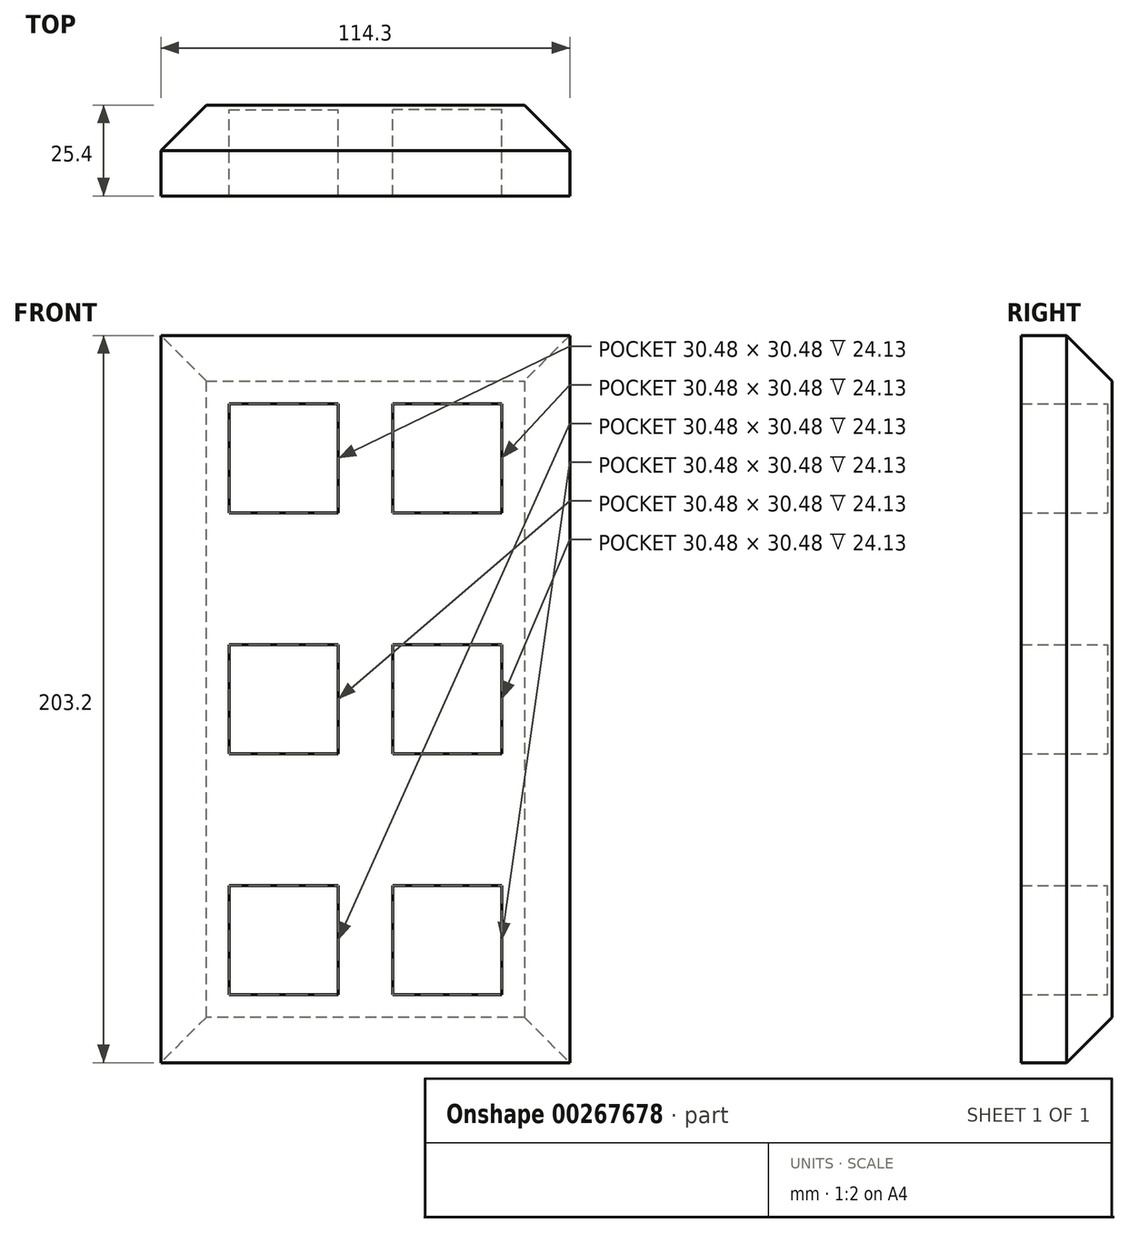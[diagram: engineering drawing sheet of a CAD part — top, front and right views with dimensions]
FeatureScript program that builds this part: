
annotation { "Feature Type Name" : "Feature", "Feature Type Description" : "" }
export const myFeature = defineFeature(function(context is Context, id is Id, definition is map)
    precondition{}
    {
        {
            var Q0;
            Q0=qCreatedBy(makeId("Front.planeOp"),FACE);
            var sketch = newSketch(context, id + "F0", { "sketchPlane" : qUnion([Q0])});
            skLineSegment(sketch, "E0.bottom", {"start": v(57.15, 101.6) * mm, "end": v(-57.15, 101.6) * mm});
            skLineSegment(sketch, "E0.top", {"start": v(57.15, -101.6) * mm, "end": v(-57.15, -101.6) * mm});
            skLineSegment(sketch, "E0.left", {"start": v(57.15, 101.6) * mm, "end": v(57.15, -101.6) * mm});
            skLineSegment(sketch, "E0.right", {"start": v(-57.15, 101.6) * mm, "end": v(-57.15, -101.6) * mm});
            skPoint(sketch, "E0.middle", {"position": v(0, 0) * mm});
            skLineSegment(sketch, "E1", {"start": v(-57.15, 101.6) * mm, "end": v(-38.1, 101.6) * mm});
            skLineSegment(sketch, "E2", {"start": v(-57.15, 101.6) * mm, "end": v(-57.15, 82.55) * mm});
            skLineSegment(sketch, "E3", {"start": v(57.15, 101.6) * mm, "end": v(38.1, 101.6) * mm});
            skLineSegment(sketch, "E4", {"start": v(57.15, 101.6) * mm, "end": v(57.15, 82.55) * mm});
            skLineSegment(sketch, "E5", {"start": v(-57.15, -101.6) * mm, "end": v(-57.15, -82.55) * mm});
            skLineSegment(sketch, "E6", {"start": v(-57.15, -101.6) * mm, "end": v(-38.1, -101.6) * mm});
            skLineSegment(sketch, "E7", {"start": v(57.15, -101.6) * mm, "end": v(57.15, -82.55) * mm});
            skLineSegment(sketch, "E8", {"start": v(57.15, -101.6) * mm, "end": v(38.1, -101.6) * mm});
            skLineSegment(sketch, "E9.bottom", {"start": v(-38.1, 82.55) * mm, "end": v(-7.62, 82.55) * mm});
            skLineSegment(sketch, "E9.top", {"start": v(-38.1, 52.07) * mm, "end": v(-7.62, 52.07) * mm});
            skLineSegment(sketch, "E9.left", {"start": v(-38.1, 82.55) * mm, "end": v(-38.1, 52.07) * mm});
            skLineSegment(sketch, "E9.right", {"start": v(-7.62, 82.55) * mm, "end": v(-7.62, 52.07) * mm});
            skLineSegment(sketch, "E10.bottom", {"start": v(38.1, 82.55) * mm, "end": v(7.62, 82.55) * mm});
            skLineSegment(sketch, "E10.top", {"start": v(38.1, 52.07) * mm, "end": v(7.62, 52.07) * mm});
            skLineSegment(sketch, "E10.left", {"start": v(38.1, 82.55) * mm, "end": v(38.1, 52.07) * mm});
            skLineSegment(sketch, "E10.right", {"start": v(7.62, 82.55) * mm, "end": v(7.62, 52.07) * mm});
            skLineSegment(sketch, "E11.bottom", {"start": v(-38.1, -82.55) * mm, "end": v(-7.62, -82.55) * mm});
            skLineSegment(sketch, "E11.top", {"start": v(-38.1, -52.07) * mm, "end": v(-7.62, -52.07) * mm});
            skLineSegment(sketch, "E11.left", {"start": v(-38.1, -82.55) * mm, "end": v(-38.1, -52.07) * mm});
            skLineSegment(sketch, "E11.right", {"start": v(-7.62, -82.55) * mm, "end": v(-7.62, -52.07) * mm});
            skLineSegment(sketch, "E12.bottom", {"start": v(38.1, -82.55) * mm, "end": v(7.62, -82.55) * mm});
            skLineSegment(sketch, "E12.top", {"start": v(38.1, -52.07) * mm, "end": v(7.62, -52.07) * mm});
            skLineSegment(sketch, "E12.left", {"start": v(38.1, -82.55) * mm, "end": v(38.1, -52.07) * mm});
            skLineSegment(sketch, "E12.right", {"start": v(7.62, -82.55) * mm, "end": v(7.62, -52.07) * mm});
            skLineSegment(sketch, "E13", {"start": v(-57.15, 0) * mm, "end": v(-38.1, 0) * mm});
            skLineSegment(sketch, "E14", {"start": v(57.15, 0) * mm, "end": v(38.1, 0) * mm});
            skLineSegment(sketch, "E15.bottom", {"start": v(-7.62, 15.24) * mm, "end": v(-38.1, 15.24) * mm});
            skLineSegment(sketch, "E15.top", {"start": v(-7.62, -15.24) * mm, "end": v(-38.1, -15.24) * mm});
            skLineSegment(sketch, "E15.left", {"start": v(-7.62, 15.24) * mm, "end": v(-7.62, -15.24) * mm});
            skLineSegment(sketch, "E15.right", {"start": v(-38.1, 15.24) * mm, "end": v(-38.1, -15.24) * mm});
            skPoint(sketch, "E15.middle", {"position": v(-22.86, 0) * mm});
            skPoint(sketch, "E15.middle.positionSnap0", {"position": v(-22.86, 52.07) * mm});
            skPoint(sketch, "E15.centerSnap0", {"position": v(-22.86, 52.07) * mm});
            skLineSegment(sketch, "E16.bottom", {"start": v(7.62, 15.24) * mm, "end": v(38.1, 15.24) * mm});
            skLineSegment(sketch, "E16.top", {"start": v(7.62, -15.24) * mm, "end": v(38.1, -15.24) * mm});
            skLineSegment(sketch, "E16.left", {"start": v(7.62, 15.24) * mm, "end": v(7.62, -15.24) * mm});
            skLineSegment(sketch, "E16.right", {"start": v(38.1, 15.24) * mm, "end": v(38.1, -15.24) * mm});
            skPoint(sketch, "E16.middle", {"position": v(22.86, 0) * mm});
            skPoint(sketch, "E16.middle.positionSnap0", {"position": v(22.86, 52.07) * mm});
            skPoint(sketch, "E16.centerSnap0", {"position": v(22.86, 52.07) * mm});
            skSolve(sketch);
        }
        {
            var Q0;
            Q0=makeQuery(id+"F0.imprint","IMPRINT",FACE,{"disambiguationData":[TD([[makeQuery(id+"F0.imprint","IMPRINT",EDGE,{"derivedFrom":sQuery(id+"F0.wireOp",EDGE,"E0.bottom")}),1.0]])]});
            extrude(context, id + "F1", {"entities" : qUnion([Q0]), "depth" : 25.4 * mm});
        }
        {
            var Q0;
            Q0=makeQuery(id+"F0.imprint","IMPRINT",FACE,{"disambiguationData":[TD([[makeQuery(id+"F0.imprint","IMPRINT",EDGE,{"derivedFrom":sQuery(id+"F0.wireOp",EDGE,"E9.bottom")}),-1.0]])]});
            var Q1;
            Q1=makeQuery(id+"F0.imprint","IMPRINT",FACE,{"disambiguationData":[TD([[makeQuery(id+"F0.imprint","IMPRINT",EDGE,{"derivedFrom":sQuery(id+"F0.wireOp",EDGE,"E10.bottom")}),1.0]])]});
            var Q2;
            {var subQ2=sQuery(id+"F0.wireOp",EDGE,"E15.bottom");Q2=makeQuery(id+"F0.imprint","IMPRINT",FACE,{"disambiguationData":[TD([[makeQuery(id+"F0.imprint","IMPRINT",EDGE,{"derivedFrom":subQ2}),1.0]])]});}
            var Q3;
            {var subQ2=sQuery(id+"F0.wireOp",EDGE,"E16.bottom");Q3=makeQuery(id+"F0.imprint","IMPRINT",FACE,{"disambiguationData":[TD([[makeQuery(id+"F0.imprint","IMPRINT",EDGE,{"derivedFrom":subQ2}),-1.0]])]});}
            var Q4;
            Q4=makeQuery(id+"F0.imprint","IMPRINT",FACE,{"disambiguationData":[TD([[makeQuery(id+"F0.imprint","IMPRINT",EDGE,{"derivedFrom":sQuery(id+"F0.wireOp",EDGE,"E11.bottom")}),1.0]])]});
            var Q5;
            Q5=makeQuery(id+"F0.imprint","IMPRINT",FACE,{"disambiguationData":[TD([[makeQuery(id+"F0.imprint","IMPRINT",EDGE,{"derivedFrom":sQuery(id+"F0.wireOp",EDGE,"E12.bottom")}),-1.0]])]});
            extrude(context, id + "F2", {"entities" : qUnion([Q0, Q1, Q2, Q3, Q4, Q5]), "operationType" : NewBodyOperationType.ADD, "depth" : 1.27 * mm});
        }
        {
            var Q0;
            Q0=makeQuery(id+"F1.opExtrude","CAP_EDGE",EDGE,{"disambiguationData":[OSD([sQuery(id+"F0.wireOp",EDGE,"E0.top"),sQuery(id+"F0.wireOp",EDGE,"E6"),sQuery(id+"F0.wireOp",EDGE,"E8")])],"isStart":true});
            chamfer(context, id + "F3", {"entities" : qUnion([Q0]), "width" : 12.7 * mm, "tangentPropagation" : true});
        }
        {
            var Q0;
            Q0=makeQuery(id+"F1.opExtrude","CAP_EDGE",EDGE,{"disambiguationData":[OSD([sQuery(id+"F0.wireOp",EDGE,"E0.right"),sQuery(id+"F0.wireOp",EDGE,"E2"),sQuery(id+"F0.wireOp",EDGE,"E5")])],"isStart":true});
            var Q1;
            Q1=makeQuery(id+"F1.opExtrude","CAP_EDGE",EDGE,{"disambiguationData":[OSD([sQuery(id+"F0.wireOp",EDGE,"E0.bottom"),sQuery(id+"F0.wireOp",EDGE,"E1"),sQuery(id+"F0.wireOp",EDGE,"E3")])],"isStart":true});
            var Q2;
            Q2=makeQuery(id+"F1.opExtrude","CAP_EDGE",EDGE,{"disambiguationData":[OSD([sQuery(id+"F0.wireOp",EDGE,"E0.left"),sQuery(id+"F0.wireOp",EDGE,"E4"),sQuery(id+"F0.wireOp",EDGE,"E7")])],"isStart":true});
            chamfer(context, id + "F4", {"entities" : qUnion([Q0, Q1, Q2]), "width" : 12.7 * mm, "tangentPropagation" : true});
        }
    });
